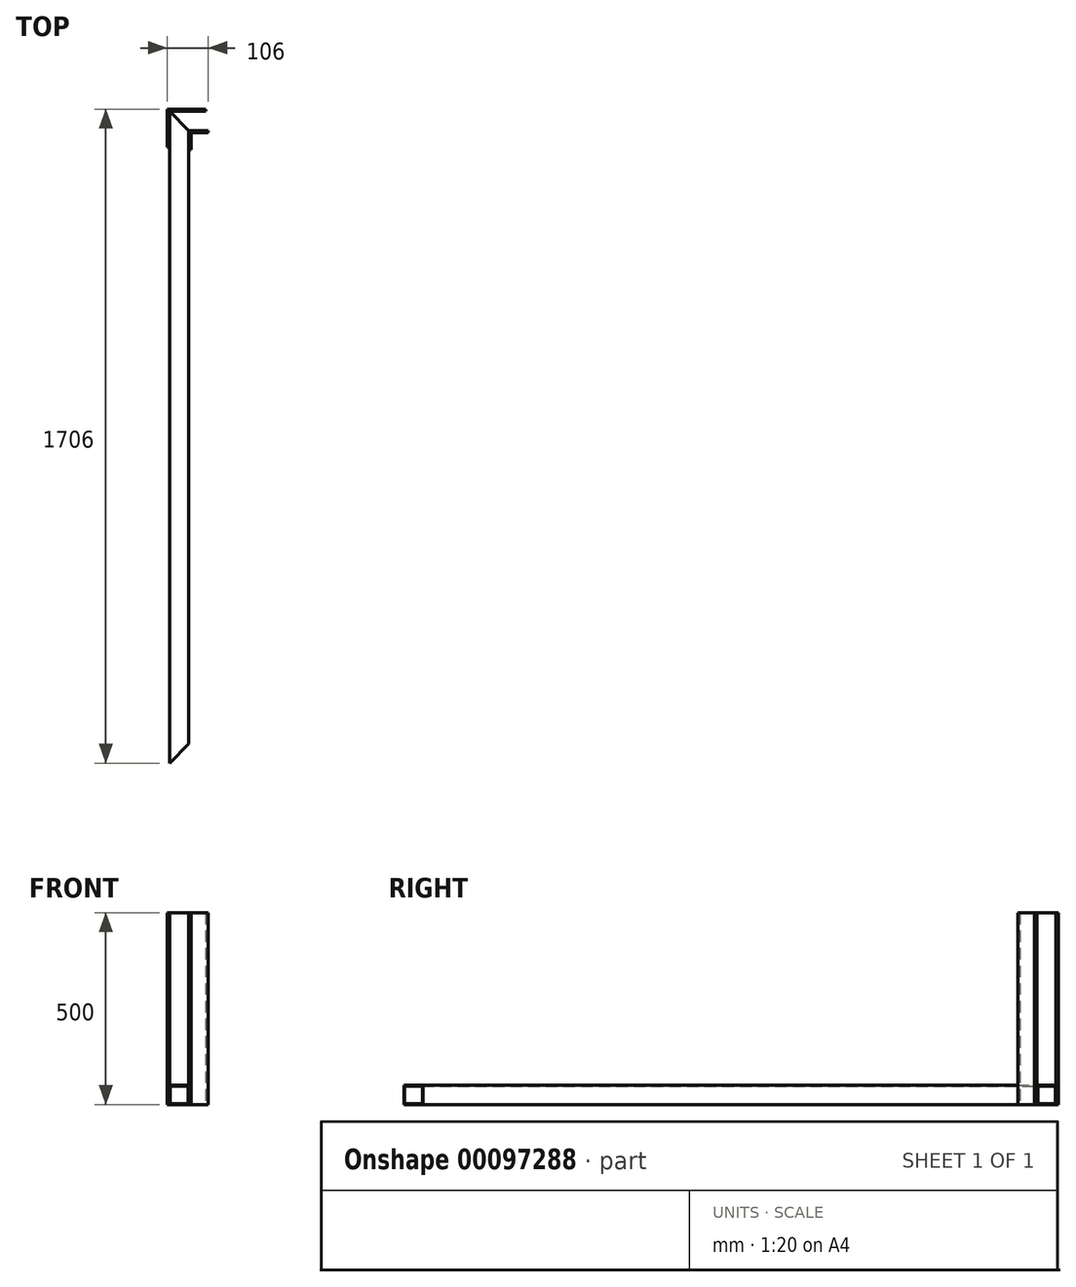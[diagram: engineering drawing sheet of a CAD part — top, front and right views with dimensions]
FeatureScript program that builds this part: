
annotation { "Feature Type Name" : "Feature", "Feature Type Description" : "" }
export const myFeature = defineFeature(function(context is Context, id is Id, definition is map)
    precondition{}
    {
        {
            var Q0;
            Q0=qCreatedBy(makeId("Front.planeOp"),FACE);
            var sketch = newSketch(context, id + "F4", { "sketchPlane" : qUnion([Q0])});
            skLineSegment(sketch, "E0.bottom", {"start": v(0, 0) * mm, "end": v(50, 0) * mm});
            skLineSegment(sketch, "E0.top", {"start": v(0, 50) * mm, "end": v(50, 50) * mm});
            skLineSegment(sketch, "E0.left", {"start": v(0, 0) * mm, "end": v(0, 50) * mm});
            skLineSegment(sketch, "E0.right", {"start": v(50, 0) * mm, "end": v(50, 50) * mm});
            skLineSegment(sketch, "E1.bottom", {"start": v(2, 2) * mm, "end": v(48, 2) * mm});
            skLineSegment(sketch, "E1.top", {"start": v(2, 48) * mm, "end": v(48, 48) * mm});
            skLineSegment(sketch, "E1.left", {"start": v(2, 2) * mm, "end": v(2, 48) * mm});
            skLineSegment(sketch, "E1.right", {"start": v(48, 2) * mm, "end": v(48, 48) * mm});
            skSolve(sketch);
        }
        {
            var Q0;
            Q0=qCreatedBy(makeId("Top.planeOp"),FACE);
            var sketch = newSketch(context, id + "F0", { "sketchPlane" : qUnion([Q0])});
            skLineSegment(sketch, "E2.bottom", {"start": v(0, 0) * mm, "end": v(51, 0) * mm});
            skLineSegment(sketch, "E2.top", {"start": v(0, -51) * mm, "end": v(51, -51) * mm});
            skLineSegment(sketch, "E2.left", {"start": v(0, 0) * mm, "end": v(0, -51) * mm});
            skLineSegment(sketch, "E2.right", {"start": v(51, 0) * mm, "end": v(51, -51) * mm});
            skLineSegment(sketch, "E3", {"start": v(0, 0) * mm, "end": v(51, -51) * mm});
            skLineSegment(sketch, "E4", {"start": v(0, -51) * mm, "end": v(51, 0) * mm});
            skSolve(sketch);
        }
        {
            var Q0;
            {var subQ0=sQuery(id+"F0.wireOp",EDGE,"5882caa5-f37b-45af-b061-dc7872925fba.bottom");Q0=makeQuery(id+"F0.imprint","IMPRINT",FACE,{"disambiguationData":[TD([[makeQuery(id+"F0.imprint","IMPRINT",EDGE,{"derivedFrom":subQ0}),-1.0]])]});}
            var Q1;
            {var subQ0=sQuery(id+"F0.wireOp",EDGE,"5882caa5-f37b-45af-b061-dc7872925fba.right");Q1=makeQuery(id+"F0.imprint","IMPRINT",FACE,{"disambiguationData":[TD([[makeQuery(id+"F0.imprint","IMPRINT",EDGE,{"derivedFrom":subQ0}),-1.0]])]});}
            var Q2;
            {var subQ0=sQuery(id+"F0.wireOp",EDGE,"E2.bottom");Q2=makeQuery(id+"F0.imprint","IMPRINT",FACE,{"disambiguationData":[TD([[makeQuery(id+"F0.imprint","IMPRINT",EDGE,{"derivedFrom":subQ0}),-1.0]])]});}
            var Q3;
            {var subQ0=sQuery(id+"F0.wireOp",EDGE,"E2.right");Q3=makeQuery(id+"F0.imprint","IMPRINT",FACE,{"disambiguationData":[TD([[makeQuery(id+"F0.imprint","IMPRINT",EDGE,{"derivedFrom":subQ0}),-1.0]])]});}
            extrude(context, id + "F5", {"entities" : qUnion([Q0, Q1, Q2, Q3]), "depth" : 50 * mm});
        }
        {
            var Q0;
            Q0=makeQuery(id+"F4.imprint","IMPRINT",FACE,{"disambiguationData":[TD([[makeQuery(id+"F4.imprint","IMPRINT",EDGE,{"derivedFrom":sQuery(id+"F4.wireOp",EDGE,"E0.bottom")}),1.0]])]});
            extrude(context, id + "F1", {"entities" : qUnion([Q0]), "depth" : 850 * mm});
        }
        {
            var Q0;
            Q0=makeQuery(id+"F5.opExtrude","SWEPT_BODY",BODY,{"disambiguationData":[OSD([sQuery(id+"F0.wireOp",EDGE,"E2.bottom"),sQuery(id+"F0.wireOp",EDGE,"E2.right"),sQuery(id+"F0.wireOp",EDGE,"E3")])]});
            var Q1;
            Q1=makeQuery(id+"F1.opExtrude","SWEPT_BODY",BODY,{"disambiguationData":[OSD([sQuery(id+"F4.wireOp",EDGE,"E0.bottom"),sQuery(id+"F4.wireOp",EDGE,"E0.top"),sQuery(id+"F4.wireOp",EDGE,"E0.left"),sQuery(id+"F4.wireOp",EDGE,"E0.right"),sQuery(id+"F4.wireOp",EDGE,"E1.bottom"),sQuery(id+"F4.wireOp",EDGE,"E1.top"),sQuery(id+"F4.wireOp",EDGE,"E1.left"),sQuery(id+"F4.wireOp",EDGE,"E1.right")])]});
            booleanBodies(context, id + "F2", {"operationType" : BooleanOperationType.SUBTRACTION, "tools" : qUnion([Q0]), "targets" : qUnion([Q1])});
        }
        {
            var Q0;
            Q0=makeQuery(id+"F1.opExtrude","SWEPT_BODY",BODY,{"disambiguationData":[OSD([sQuery(id+"F4.wireOp",EDGE,"E0.bottom"),sQuery(id+"F4.wireOp",EDGE,"E0.top"),sQuery(id+"F4.wireOp",EDGE,"E0.left"),sQuery(id+"F4.wireOp",EDGE,"E0.right"),sQuery(id+"F4.wireOp",EDGE,"E1.bottom"),sQuery(id+"F4.wireOp",EDGE,"E1.top"),sQuery(id+"F4.wireOp",EDGE,"E1.left"),sQuery(id+"F4.wireOp",EDGE,"E1.right")])]});
            var Q1;
            Q1=makeQuery(id+"F1.opExtrude","CAP_FACE",FACE,{"disambiguationData":[OSD([sQuery(id+"F4.wireOp",EDGE,"E0.bottom"),sQuery(id+"F4.wireOp",EDGE,"E0.top"),sQuery(id+"F4.wireOp",EDGE,"E0.left"),sQuery(id+"F4.wireOp",EDGE,"E0.right"),sQuery(id+"F4.wireOp",EDGE,"E1.bottom"),sQuery(id+"F4.wireOp",EDGE,"E1.top"),sQuery(id+"F4.wireOp",EDGE,"E1.left"),sQuery(id+"F4.wireOp",EDGE,"E1.right")])],"isStart":false});
            mirror(context, id + "F6", {"operationType" : NewBodyOperationType.ADD, "entities" : qUnion([Q0]), "mirrorPlane" : qUnion([Q1])});
        }
        {
            var Q0;
            Q0=qCreatedBy(makeId("Top.planeOp"),FACE);
            var sketch = newSketch(context, id + "F3", { "sketchPlane" : qUnion([Q0])});
            skLineSegment(sketch, "E5.bottom", {"start": v(0, 0) * mm, "end": v(94, 0) * mm});
            skLineSegment(sketch, "E5.top", {"start": v(0, -94) * mm, "end": v(94, -94) * mm});
            skLineSegment(sketch, "E5.left", {"start": v(0, 0) * mm, "end": v(0, -94) * mm});
            skLineSegment(sketch, "E5.right", {"start": v(94, 0) * mm, "end": v(94, -94) * mm});
            skLineSegment(sketch, "E6.bottom", {"start": v(94, -94) * mm, "end": v(-6, -94) * mm});
            skLineSegment(sketch, "E6.top", {"start": v(94, 6) * mm, "end": v(-6, 6) * mm});
            skLineSegment(sketch, "E6.left", {"start": v(94, -94) * mm, "end": v(94, 6) * mm});
            skLineSegment(sketch, "E6.right", {"start": v(-6, -94) * mm, "end": v(-6, 6) * mm});
            skLineSegment(sketch, "E7.bottom", {"start": v(100, -100) * mm, "end": v(50, -100) * mm});
            skLineSegment(sketch, "E7.top", {"start": v(100, -50) * mm, "end": v(50, -50) * mm});
            skLineSegment(sketch, "E7.left", {"start": v(100, -100) * mm, "end": v(100, -50) * mm});
            skLineSegment(sketch, "E7.right", {"start": v(50, -100) * mm, "end": v(50, -50) * mm});
            skLineSegment(sketch, "E8.bottom", {"start": v(100, -100) * mm, "end": v(56, -100) * mm});
            skLineSegment(sketch, "E8.top", {"start": v(100, -56) * mm, "end": v(56, -56) * mm});
            skLineSegment(sketch, "E8.left", {"start": v(100, -100) * mm, "end": v(100, -56) * mm});
            skLineSegment(sketch, "E8.right", {"start": v(56, -100) * mm, "end": v(56, -56) * mm});
            skSolve(sketch);
        }
        {
            var Q0;
            {var subQ5=sQuery(id+"F3.wireOp",EDGE,"E8.right");var subQ6=sQuery(id+"F3.wireOp",EDGE,"E5.top");var subQ7=makeQuery(id+"F3.imprint","INTERSECT",VERTEX,{"derivedFrom":[subQ6,subQ5]});Q0=makeQuery(id+"F3.imprint","IMPRINT",FACE,{"disambiguationData":[TD([[makeQuery(id+"F3.imprint","IMPRINT",EDGE,{"disambiguationData":[TD([[subQ7,1.0]])],"derivedFrom":subQ6}),1.0]])]});}
            var Q1;
            {var subQ0=sQuery(id+"F3.wireOp",EDGE,"E8.right");var subQ1=sQuery(id+"F3.wireOp",EDGE,"E5.top");var subQ2=makeQuery(id+"F3.imprint","INTERSECT",VERTEX,{"derivedFrom":[subQ1,subQ0]});Q1=makeQuery(id+"F3.imprint","IMPRINT",FACE,{"disambiguationData":[TD([[makeQuery(id+"F3.imprint","IMPRINT",EDGE,{"disambiguationData":[TD([[subQ2,1.0]])],"derivedFrom":subQ1}),-1.0]])]});}
            var Q2;
            {var subQ0=sQuery(id+"F3.wireOp",EDGE,"E8.top");var subQ1=sQuery(id+"F3.wireOp",EDGE,"E5.right");var subQ2=makeQuery(id+"F3.imprint","INTERSECT",VERTEX,{"derivedFrom":[subQ1,subQ0]});Q2=makeQuery(id+"F3.imprint","IMPRINT",FACE,{"disambiguationData":[TD([[makeQuery(id+"F3.imprint","IMPRINT",EDGE,{"disambiguationData":[TD([[subQ2,1.0]])],"derivedFrom":subQ1}),1.0]])]});}
            var Q3;
            Q3=makeQuery(id+"F3.imprint","IMPRINT",FACE,{"disambiguationData":[TD([[makeQuery(id+"F3.imprint","IMPRINT",EDGE,{"derivedFrom":sQuery(id+"F3.wireOp",EDGE,"E5.bottom")}),1.0]])]});
            extrude(context, id + "F7", {"entities" : qUnion([Q0, Q1, Q2, Q3]), "depth" : 500 * mm});
        }
    });
